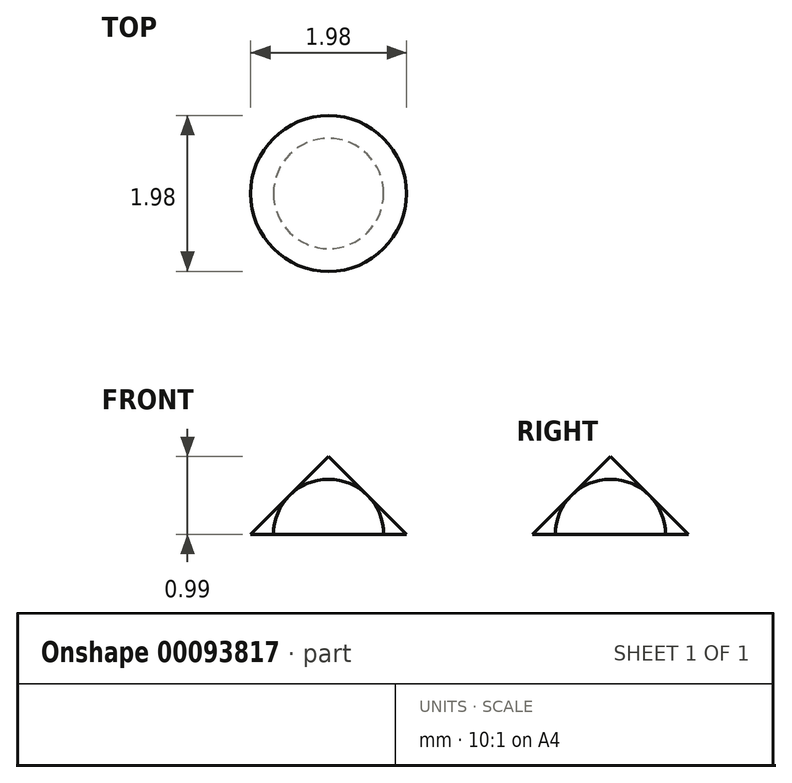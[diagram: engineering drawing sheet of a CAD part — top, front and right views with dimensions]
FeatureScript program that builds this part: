
annotation { "Feature Type Name" : "Feature", "Feature Type Description" : "" }
export const myFeature = defineFeature(function(context is Context, id is Id, definition is map)
    precondition{}
    {
        {
            var Q0;
            Q0=qCreatedBy(makeId("Front.planeOp"),FACE);
            var sketch = newSketch(context, id + "F0", { "sketchPlane" : qUnion([Q0])});
            skArc(sketch, "E0", {"start": v(0.7, 0) * mm, "mid": v(0.5, 0.5) * mm, "end": v(0, 0.7) * mm});
            skLineSegment(sketch, "E1", {"start": v(0, 0) * mm, "end": v(0.7, 0) * mm});
            skLineSegment(sketch, "E2", {"start": v(0, 0) * mm, "end": v(0, 0.7) * mm});
            skLineSegment(sketch, "E3", {"start": v(0, 0.99) * mm, "end": v(0.99, 0) * mm});
            skLineSegment(sketch, "E4", {"start": v(0, 0.99) * mm, "end": v(0, 0) * mm});
            skLineSegment(sketch, "E5", {"start": v(0.99, 0) * mm, "end": v(0, 0) * mm});
            skSolve(sketch);
        }
        {
            var Q0;
            Q0=makeQuery(id+"F0.imprint","IMPRINT",FACE,{"disambiguationData":[TD([[makeQuery(id+"F0.imprint","IMPRINT",EDGE,{"derivedFrom":sQuery(id+"F0.wireOp",EDGE,"E0")}),1.0]])]});
            var Q1;
            Q1=sQuery(id+"F0.wireOp",EDGE,"E2");
            revolve(context, id + "F1", {"entities" : qUnion([Q0]), "axis" : qUnion([Q1]), "revolveType" : RevolveType.FULL});
        }
        {
            var Q0;
            {var subQ0=sQuery(id+"F0.wireOp",EDGE,"E4");var subQ3=sQuery(id+"F0.wireOp",EDGE,"E0");var subQ4=makeQuery(id+"F0.imprint","INTERSECT",VERTEX,{"derivedFrom":[subQ3,subQ0]});Q0=makeQuery(id+"F0.imprint","IMPRINT",FACE,{"disambiguationData":[TD([[makeQuery(id+"F0.imprint","IMPRINT",EDGE,{"disambiguationData":[TD([[subQ4,1.0]])],"derivedFrom":subQ3}),-1.0]])]});}
            var Q1;
            {var subQ0=sQuery(id+"F0.wireOp",EDGE,"E5");var subQ3=sQuery(id+"F0.wireOp",EDGE,"E0");var subQ4=makeQuery(id+"F0.imprint","INTERSECT",VERTEX,{"derivedFrom":[subQ3,subQ0]});Q1=makeQuery(id+"F0.imprint","IMPRINT",FACE,{"disambiguationData":[TD([[makeQuery(id+"F0.imprint","IMPRINT",EDGE,{"disambiguationData":[TD([[subQ4,-1.0]])],"derivedFrom":subQ3}),-1.0]])]});}
            var Q2;
            {var subQ0=sQuery(id+"F0.wireOp",EDGE,"E5");var subQ3=sQuery(id+"F0.wireOp",EDGE,"E0");var subQ4=makeQuery(id+"F0.imprint","INTERSECT",VERTEX,{"derivedFrom":[subQ3,subQ0]});Q2=makeQuery(id+"F0.imprint","IMPRINT",FACE,{"disambiguationData":[TD([[makeQuery(id+"F0.imprint","IMPRINT",EDGE,{"disambiguationData":[TD([[subQ4,-1.0]])],"derivedFrom":subQ3}),1.0]])]});}
            var Q3;
            Q3=sQuery(id+"F0.wireOp",EDGE,"E4");
            revolve(context, id + "F2", {"entities" : qUnion([Q0, Q1, Q2]), "axis" : qUnion([Q3]), "revolveType" : RevolveType.FULL});
        }
    });
